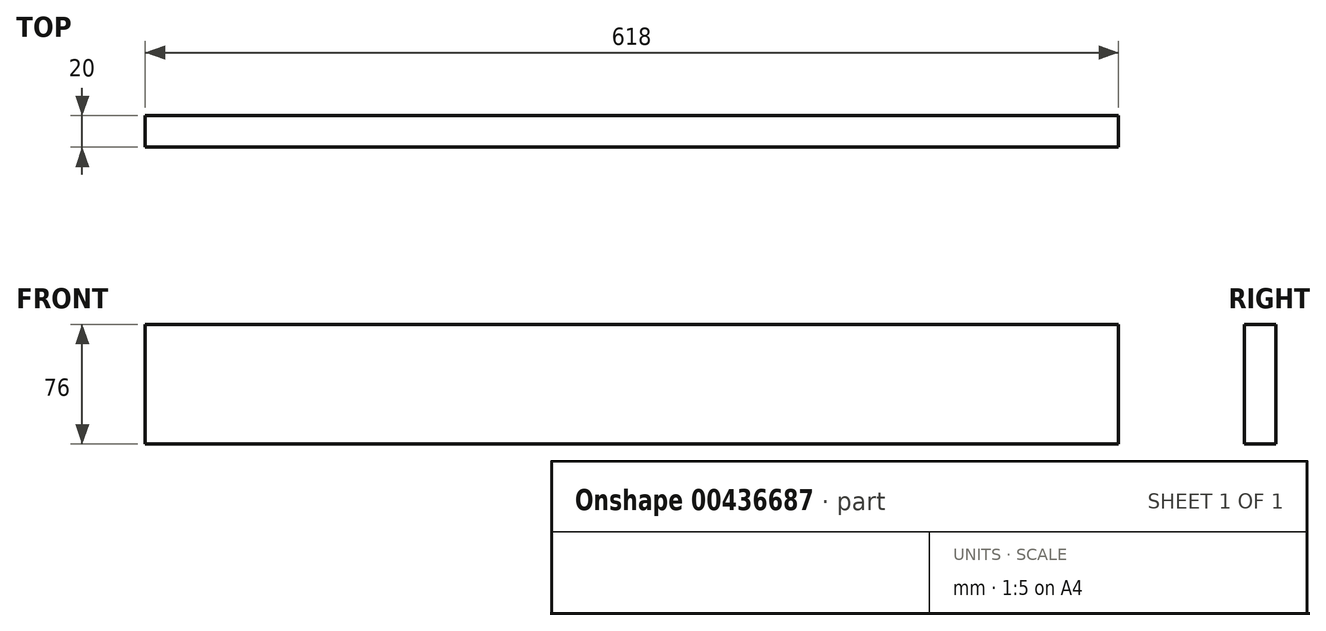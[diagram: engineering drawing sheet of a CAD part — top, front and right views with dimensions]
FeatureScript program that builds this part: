
annotation { "Feature Type Name" : "Feature", "Feature Type Description" : "" }
export const myFeature = defineFeature(function(context is Context, id is Id, definition is map)
    precondition{}
    {
        {
            var Q0;
            Q0=qCreatedBy(makeId("Right.planeOp"),FACE);
            var sketch = newSketch(context, id + "F0", { "sketchPlane" : qUnion([Q0])});
            skLineSegment(sketch, "E0.bottom", {"start": v(10, 38) * mm, "end": v(-10, 38) * mm});
            skLineSegment(sketch, "E0.top", {"start": v(10, -38) * mm, "end": v(-10, -38) * mm});
            skLineSegment(sketch, "E0.left", {"start": v(10, 38) * mm, "end": v(10, -38) * mm});
            skLineSegment(sketch, "E0.right", {"start": v(-10, 38) * mm, "end": v(-10, -38) * mm});
            skPoint(sketch, "E0.middle", {"position": v(0, 0) * mm});
            skSolve(sketch);
        }
        {
            var Q0;
            Q0=qSketchRegion(id+"F0",true);
            extrude(context, id + "F1", {"entities" : qUnion([Q0]), "depth" : 618 * mm});
        }
    });
